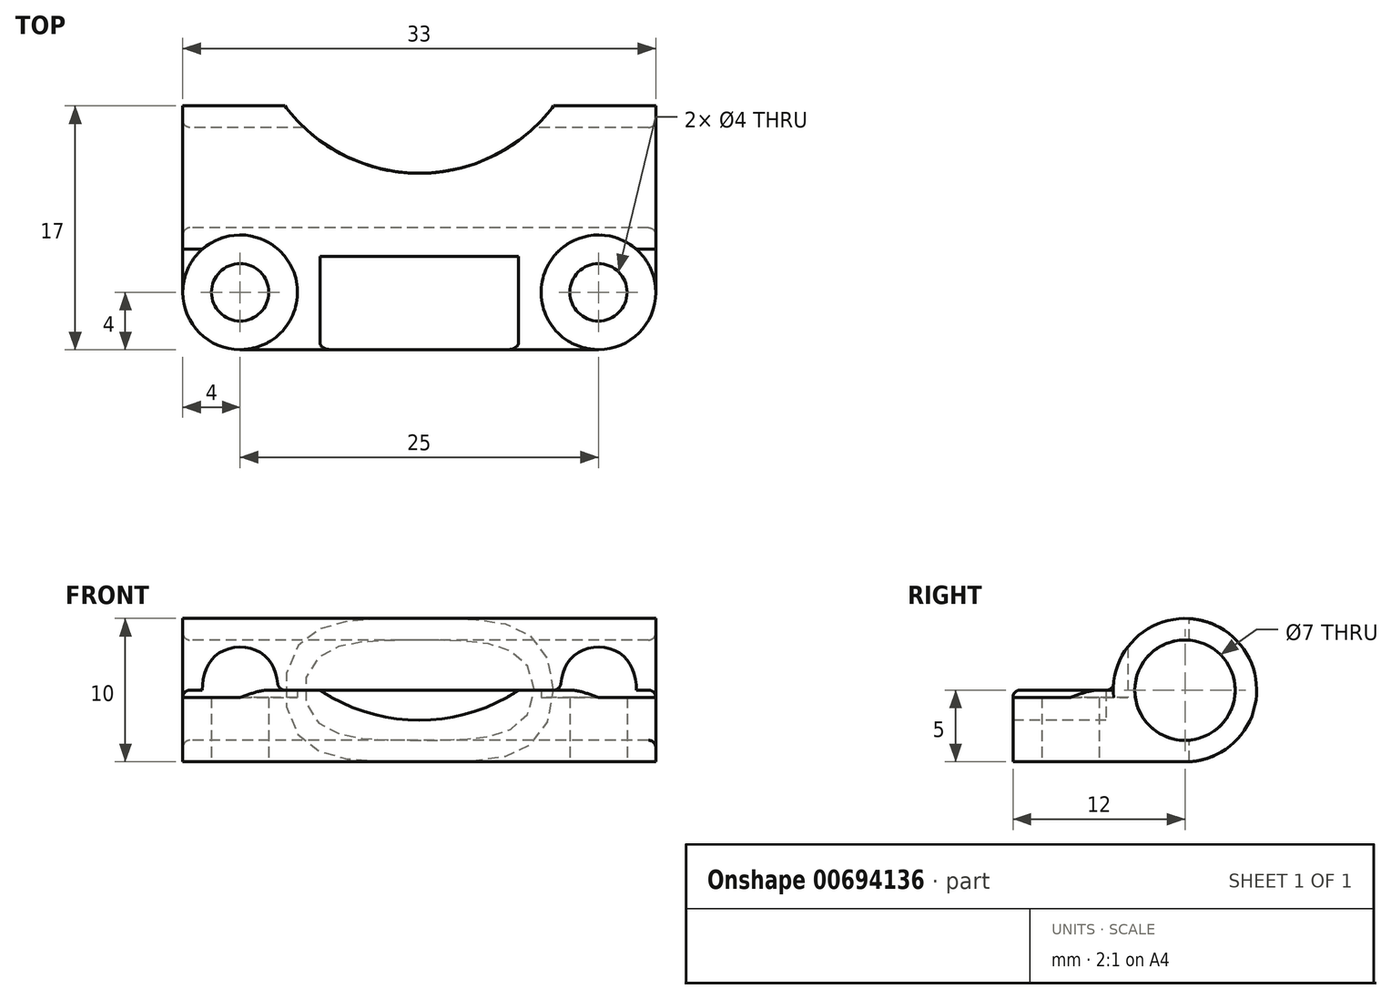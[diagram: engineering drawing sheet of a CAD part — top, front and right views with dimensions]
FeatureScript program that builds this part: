
annotation { "Feature Type Name" : "Feature", "Feature Type Description" : "" }
export const myFeature = defineFeature(function(context is Context, id is Id, definition is map)
    precondition{}
    {
        {
            var Q0;
            Q0=qCreatedBy(makeId("Top.planeOp"),FACE);
            var sketch = newSketch(context, id + "F0", { "sketchPlane" : qUnion([Q0])});
            skLineSegment(sketch, "E0", {"start": v(0, 0) * mm, "end": v(-12.5, 0) * mm, "construction": true});
            skCircle(sketch, "E1", {"center": v(-12.5, 0) * mm, "radius": 2 * mm});
            skArc(sketch, "E2", {"start": v(-12.5, -4) * mm, "mid": v(-15.33, -2.83) * mm, "end": v(-16.5, 0) * mm});
            skLineSegment(sketch, "E3", {"start": v(-12.5, -4) * mm, "end": v(0, -4) * mm});
            skLineSegment(sketch, "E4", {"start": v(-16.5, 0) * mm, "end": v(-16.5, 8) * mm});
            skLineSegment(sketch, "E5", {"start": v(-16.5, 8) * mm, "end": v(0, 8) * mm});
            skLineSegment(sketch, "E6.MirrorCS", {"start": v(12.5, -4) * mm, "end": v(0, -4) * mm});
            skArc(sketch, "E7.MirrorCS", {"start": v(12.5, -4) * mm, "mid": v(15.33, -2.83) * mm, "end": v(16.5, 0) * mm});
            skLineSegment(sketch, "E8.MirrorCS", {"start": v(16.5, 0) * mm, "end": v(16.5, 8) * mm});
            skLineSegment(sketch, "E9.MirrorCS", {"start": v(16.5, 8) * mm, "end": v(0, 8) * mm});
            skCircle(sketch, "E10.MirrorC", {"center": v(12.5, 0) * mm, "radius": 2 * mm});
            skSolve(sketch);
        }
        {
            var Q0;
            Q0=makeQuery(id+"F0.imprint","IMPRINT",FACE,{"disambiguationData":[TD([[makeQuery(id+"F0.imprint","IMPRINT",EDGE,{"derivedFrom":sQuery(id+"F0.wireOp",EDGE,"E1")}),-1.0]])]});
            extrude(context, id + "F1", {"entities" : qUnion([Q0]), "depth" : 5 * mm, "offsetDistance" : 25 * mm});
        }
        {
            var Q0;
            Q0=qCreatedBy(makeId("Right.planeOp"),FACE);
            var sketch = newSketch(context, id + "F2", { "sketchPlane" : qUnion([Q0])});
            skLineSegment(sketch, "E11", {"start": v(0, 0) * mm, "end": v(8, 0) * mm, "construction": true});
            skLineSegment(sketch, "E12", {"start": v(8, 0) * mm, "end": v(8, 4) * mm, "construction": true});
            skLineSegment(sketch, "E13", {"start": v(8, 4) * mm, "end": v(16.15, 4) * mm, "construction": true});
            skCircle(sketch, "E14", {"center": v(8, 5) * mm, "radius": 5 * mm});
            skCircle(sketch, "E15", {"center": v(8, 5) * mm, "radius": 3.5 * mm});
            skSolve(sketch);
        }
        {
            var Q0;
            Q0=makeQuery(id+"F2.imprint","IMPRINT",FACE,{"disambiguationData":[TD([[makeQuery(id+"F2.imprint","IMPRINT",EDGE,{"derivedFrom":sQuery(id+"F2.wireOp",EDGE,"E14")}),1.0]])]});
            extrude(context, id + "F3", {"entities" : qUnion([Q0]), "operationType" : NewBodyOperationType.ADD, "depth" : 16.5 * mm, "offsetDistance" : 25 * mm, "hasSecondDirection" : true, "secondDirectionOppositeDirection" : true, "secondDirectionDepth" : 16.5 * mm});
        }
        {
            var Q0;
            Q0=makeQuery(id+"F2.imprint","IMPRINT",FACE,{"disambiguationData":[TD([[makeQuery(id+"F2.imprint","IMPRINT",EDGE,{"derivedFrom":sQuery(id+"F2.wireOp",EDGE,"E15")}),1.0]])]});
            extrude(context, id + "F4", {"entities" : qUnion([Q0]), "operationType" : NewBodyOperationType.REMOVE, "oppositeDirection" : true, "depth" : 25 * mm, "offsetDistance" : 25 * mm, "hasSecondDirection" : true, "secondDirectionOppositeDirection" : false, "secondDirectionDepth" : 25 * mm});
        }
        {
            var Q0;
            Q0=qCreatedBy(makeId("Top.planeOp"),FACE);
            var sketch = newSketch(context, id + "F5", { "sketchPlane" : qUnion([Q0])});
            skLineSegment(sketch, "E16", {"start": v(0, 0) * mm, "end": v(-12.5, 0) * mm, "construction": true});
            skCircle(sketch, "E17", {"center": v(-12.5, 0) * mm, "radius": 4 * mm});
            skCircle(sketch, "E18.MirrorC", {"center": v(12.5, 0) * mm, "radius": 4 * mm});
            skSolve(sketch);
        }
        {
            var Q0;
            Q0 = qSketchRegion(id + "F5", true);
            extrude(context, id + "F6", {"entities" : qUnion([Q0]), "operationType" : NewBodyOperationType.REMOVE, "depth" : 25 * mm, "offsetDistance" : 25 * mm, "hasSecondDirection" : true, "secondDirectionOppositeDirection" : false, "secondDirectionDepth" : 4.5 * mm});
        }
        {
            var Q0;
            {var subQ0=sQuery(id+"F2.wireOp",EDGE,"E15");Q0=makeQuery(id+"F4.boolean.opBoolean","INTERSECT",EDGE,{"derivedFrom":[makeQuery(id+"F3.boolean.opBoolean","MERGE",FACE,{"derivedFrom":[makeQuery(id+"F1.opExtrude","SWEPT_FACE",FACE,{"disambiguationData":[OSD([sQuery(id+"F0.wireOp",EDGE,"E4")])]}),makeQuery(id+"F3.opExtrude","CAP_FACE",FACE,{"disambiguationData":[OSD([sQuery(id+"F2.wireOp",EDGE,"E14"),subQ0])],"isStart":true})]}),makeQuery(id+"F4.opExtrude","SWEPT_FACE",FACE,{"disambiguationData":[OSD([subQ0])]})]});}
            var Q1;
            {var subQ0=sQuery(id+"F2.wireOp",EDGE,"E15");Q1=makeQuery(id+"F4.boolean.opBoolean","INTERSECT",EDGE,{"derivedFrom":[makeQuery(id+"F3.boolean.opBoolean","MERGE",FACE,{"derivedFrom":[makeQuery(id+"F1.opExtrude","SWEPT_FACE",FACE,{"disambiguationData":[OSD([sQuery(id+"F0.wireOp",EDGE,"E8.MirrorCS")])]}),makeQuery(id+"F3.opExtrude","CAP_FACE",FACE,{"disambiguationData":[OSD([sQuery(id+"F2.wireOp",EDGE,"E14"),subQ0])],"isStart":false})]}),makeQuery(id+"F4.opExtrude","SWEPT_FACE",FACE,{"disambiguationData":[OSD([subQ0])]})]});}
            var Q2;
            Q2=makeQuery(id+"F1.opExtrude","CAP_EDGE",EDGE,{"disambiguationData":[OSD([sQuery(id+"F0.wireOp",EDGE,"E3"),sQuery(id+"F0.wireOp",EDGE,"E6.MirrorCS")])],"isStart":false});
            var Q3;
            {var subQ0=makeQuery(id+"F1.opExtrude","CAP_FACE",FACE,{"disambiguationData":[OSD([sQuery(id+"F0.wireOp",EDGE,"E1"),sQuery(id+"F0.wireOp",EDGE,"E2"),sQuery(id+"F0.wireOp",EDGE,"E3"),sQuery(id+"F0.wireOp",EDGE,"E4"),sQuery(id+"F0.wireOp",EDGE,"E5"),sQuery(id+"F0.wireOp",EDGE,"E6.MirrorCS"),sQuery(id+"F0.wireOp",EDGE,"E7.MirrorCS"),sQuery(id+"F0.wireOp",EDGE,"E8.MirrorCS"),sQuery(id+"F0.wireOp",EDGE,"E9.MirrorCS"),sQuery(id+"F0.wireOp",EDGE,"E10.MirrorC")])],"isStart":false});var subQ1=makeQuery(id+"F3.opExtrude","SWEPT_FACE",FACE,{"disambiguationData":[OSD([sQuery(id+"F2.wireOp",EDGE,"E14")])]});Q3=makeQuery(id+"F6.boolean.opBoolean","SPLIT",EDGE,{"disambiguationData":[TD([subQ0,subQ1,makeQuery(id+"F6.opExtrude","SWEPT_FACE",FACE,{"disambiguationData":[OSD([sQuery(id+"F5.wireOp",EDGE,"E17")])]}),makeQuery(id+"F6.opExtrude","SWEPT_FACE",FACE,{"disambiguationData":[OSD([sQuery(id+"F5.wireOp",EDGE,"E18.MirrorC")])]})])],"derivedFrom":makeQuery(id+"F3.boolean.opBoolean","INTERSECT",EDGE,{"derivedFrom":[subQ0,subQ1]})});}
            var Q4;
            {var subQ1=sQuery(id+"F0.wireOp",EDGE,"E8.MirrorCS");var subQ2=sQuery(id+"F0.wireOp",EDGE,"E7.MirrorCS");Q4=makeQuery(id+"F3.boolean.opBoolean","SPLIT",EDGE,{"disambiguationData":[TD([makeQuery(id+"F1.opExtrude","SWEPT_FACE",FACE,{"disambiguationData":[OSD([subQ2])]})])],"derivedFrom":makeQuery(id+"F1.opExtrude","CAP_EDGE",EDGE,{"disambiguationData":[OSD([subQ1])],"isStart":false})});}
            var Q5;
            {var subQ0=sQuery(id+"F0.wireOp",EDGE,"E4");var subQ2=sQuery(id+"F0.wireOp",EDGE,"E2");Q5=makeQuery(id+"F3.boolean.opBoolean","SPLIT",EDGE,{"disambiguationData":[TD([makeQuery(id+"F1.opExtrude","SWEPT_FACE",FACE,{"disambiguationData":[OSD([subQ2])]})])],"derivedFrom":makeQuery(id+"F1.opExtrude","CAP_EDGE",EDGE,{"disambiguationData":[OSD([subQ0])],"isStart":false})});}
            fillet(context, id + "F7", {"entities" : qUnion([Q0, Q1, Q2, Q3, Q4, Q5]), "radius" : .5 * mm, "tangentPropagation" : true, "allowEdgeOverflow" : false});
        }
        {
            var Q0;
            Q0=qCreatedBy(makeId("Top.planeOp"),FACE);
            var sketch = newSketch(context, id + "F8", { "sketchPlane" : qUnion([Q0])});
            skLineSegment(sketch, "E19", {"start": v(0, 0) * mm, "end": v(0, 20) * mm, "construction": true});
            skCircle(sketch, "E20", {"center": v(0, 20) * mm, "radius": 11.7 * mm});
            skSolve(sketch);
        }
        {
            var Q0;
            Q0=makeQuery(id+"F8.imprint","IMPRINT",FACE,{"disambiguationData":[TD([[makeQuery(id+"F8.imprint","IMPRINT",EDGE,{"derivedFrom":sQuery(id+"F8.wireOp",EDGE,"E20")}),1.0]])]});
            extrude(context, id + "F9", {"entities" : qUnion([Q0]), "operationType" : NewBodyOperationType.REMOVE, "oppositeDirection" : true, "depth" : 25 * mm, "offsetDistance" : 25 * mm, "hasSecondDirection" : true, "secondDirectionOppositeDirection" : false, "secondDirectionDepth" : 25 * mm});
        }
        {
            var Q0;
            Q0=qCreatedBy(makeId("Front.planeOp"),FACE);
            var sketch = newSketch(context, id + "F10", { "sketchPlane" : qUnion([Q0])});
            skLineSegment(sketch, "E21", {"start": v(0, 1.4) * mm, "end": v(0, 15.4) * mm, "construction": true});
            skCircle(sketch, "E22", {"center": v(0, 15.4) * mm, "radius": 12.5 * mm});
            skSolve(sketch);
        }
        {
            var Q0;
            Q0=makeQuery(id+"F10.imprint","IMPRINT",FACE,{"disambiguationData":[TD([[makeQuery(id+"F10.imprint","IMPRINT",EDGE,{"derivedFrom":sQuery(id+"F10.wireOp",EDGE,"E22")}),1.0]])]});
            extrude(context, id + "F11", {"entities" : qUnion([Q0]), "operationType" : NewBodyOperationType.REMOVE, "oppositeDirection" : true, "depth" : 2.5 * mm, "offsetDistance" : 25 * mm, "hasSecondDirection" : true, "secondDirectionOppositeDirection" : false, "secondDirectionDepth" : 25 * mm});
        }
    });
